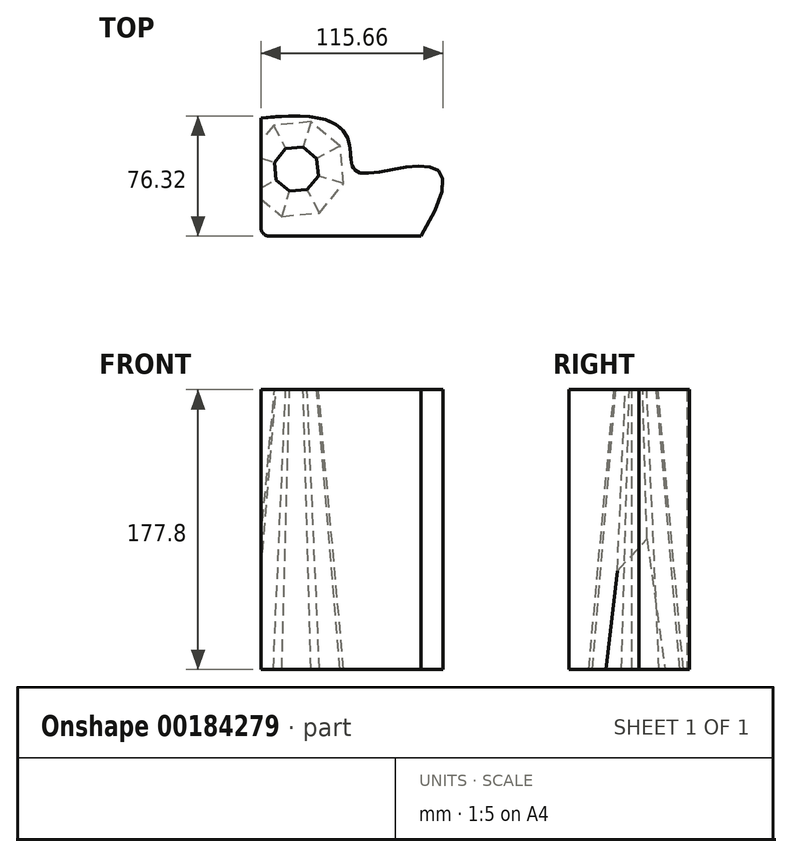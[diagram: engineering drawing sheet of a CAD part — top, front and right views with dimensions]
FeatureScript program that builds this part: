
annotation { "Feature Type Name" : "Feature", "Feature Type Description" : "" }
export const myFeature = defineFeature(function(context is Context, id is Id, definition is map)
    precondition{}
    {
        {
            var Q0;
            Q0=qCreatedBy(makeId("Top.planeOp"),FACE);
            var sketch = newSketch(context, id + "F0", { "sketchPlane" : qUnion([Q0])});
            skLineSegment(sketch, "E0", {"start": v(37, -39.92) * mm, "end": v(-59.52, -39.92) * mm});
            skLineSegment(sketch, "E1", {"start": v(-64.6, -34.84) * mm, "end": v(-64.6, 35) * mm});
            skFitSpline(sketch, "E2", {"points": [v(-64.6, 35) * mm, v(0, 0) * mm, v(37, -39.92) * mm], "startDerivative": vector(454.61, 53.15) * mm, "endDerivative": vector(-266.86, -432.3) * mm});
            skPoint(sketch, "E3.visualSharp", {"position": v(-64.6, -39.92) * mm});
            skArc(sketch, "E3.filletArc", {"start": v(-64.6, -34.84) * mm, "mid": v(-63.11, -38.43) * mm, "end": v(-59.52, -39.92) * mm});
            skSolve(sketch);
        }
        {
            var Q0;
            Q0=makeQuery(id+"F0.imprint","IMPRINT",FACE,{"disambiguationData":[TD([[makeQuery(id+"F0.imprint","IMPRINT",EDGE,{"derivedFrom":sQuery(id+"F0.wireOp",EDGE,"E0")}),-1.0]])]});
            extrude(context, id + "F1", {"entities" : qUnion([Q0]), "depth" : 177.8 * mm});
        }
        {
            var Q0;
            Q0=makeQuery(id+"F1.opExtrude","CAP_FACE",FACE,{"disambiguationData":[OSD([sQuery(id+"F0.wireOp",EDGE,"E0"),sQuery(id+"F0.wireOp",EDGE,"E1"),sQuery(id+"F0.wireOp",EDGE,"E2"),sQuery(id+"F0.wireOp",EDGE,"E3.filletArc")])],"isStart":false});
            var sketch = newSketch(context, id + "F2", { "sketchPlane" : qUnion([Q0])});
            skCircle(sketch, "E4.cCircle", {"center": v(-42.08, 2.67) * mm, "radius": 13.47 * mm, "construction": true});
            skLineSegment(sketch, "E4.0", {"start": v(-28.15, -1.63) * mm, "end": v(-35.27, -10.22) * mm});
            skLineSegment(sketch, "E4.1", {"start": v(-35.27, -10.22) * mm, "end": v(-46.38, -11.26) * mm});
            skLineSegment(sketch, "E4.2", {"start": v(-46.38, -11.26) * mm, "end": v(-54.97, -4.15) * mm});
            skLineSegment(sketch, "E4.3", {"start": v(-54.97, -4.15) * mm, "end": v(-56.01, 6.96) * mm});
            skLineSegment(sketch, "E4.4", {"start": v(-56.01, 6.96) * mm, "end": v(-48.9, 15.56) * mm});
            skLineSegment(sketch, "E4.5", {"start": v(-48.9, 15.56) * mm, "end": v(-37.78, 16.6) * mm});
            skLineSegment(sketch, "E4.6", {"start": v(-37.78, 16.6) * mm, "end": v(-29.19, 9.48) * mm});
            skLineSegment(sketch, "E4.7", {"start": v(-29.19, 9.48) * mm, "end": v(-28.15, -1.63) * mm});
            skPoint(sketch, "E4.0.midPoint", {"position": v(-31.7, -5.93) * mm});
            skSolve(sketch);
        }
        {
            var Q0;
            Q0=makeQuery(id+"F2.imprint","IMPRINT",FACE,{"disambiguationData":[TD([[makeQuery(id+"F2.imprint","IMPRINT",EDGE,{"derivedFrom":sQuery(id+"F2.wireOp",EDGE,"E4.0")}),-1.0]])]});
            extrude(context, id + "F3", {"entities" : qUnion([Q0]), "operationType" : NewBodyOperationType.REMOVE, "oppositeDirection" : true, "depth" : 254 * mm, "hasDraft" : true, "draftAngle" : 5 * degree});
        }
    });
